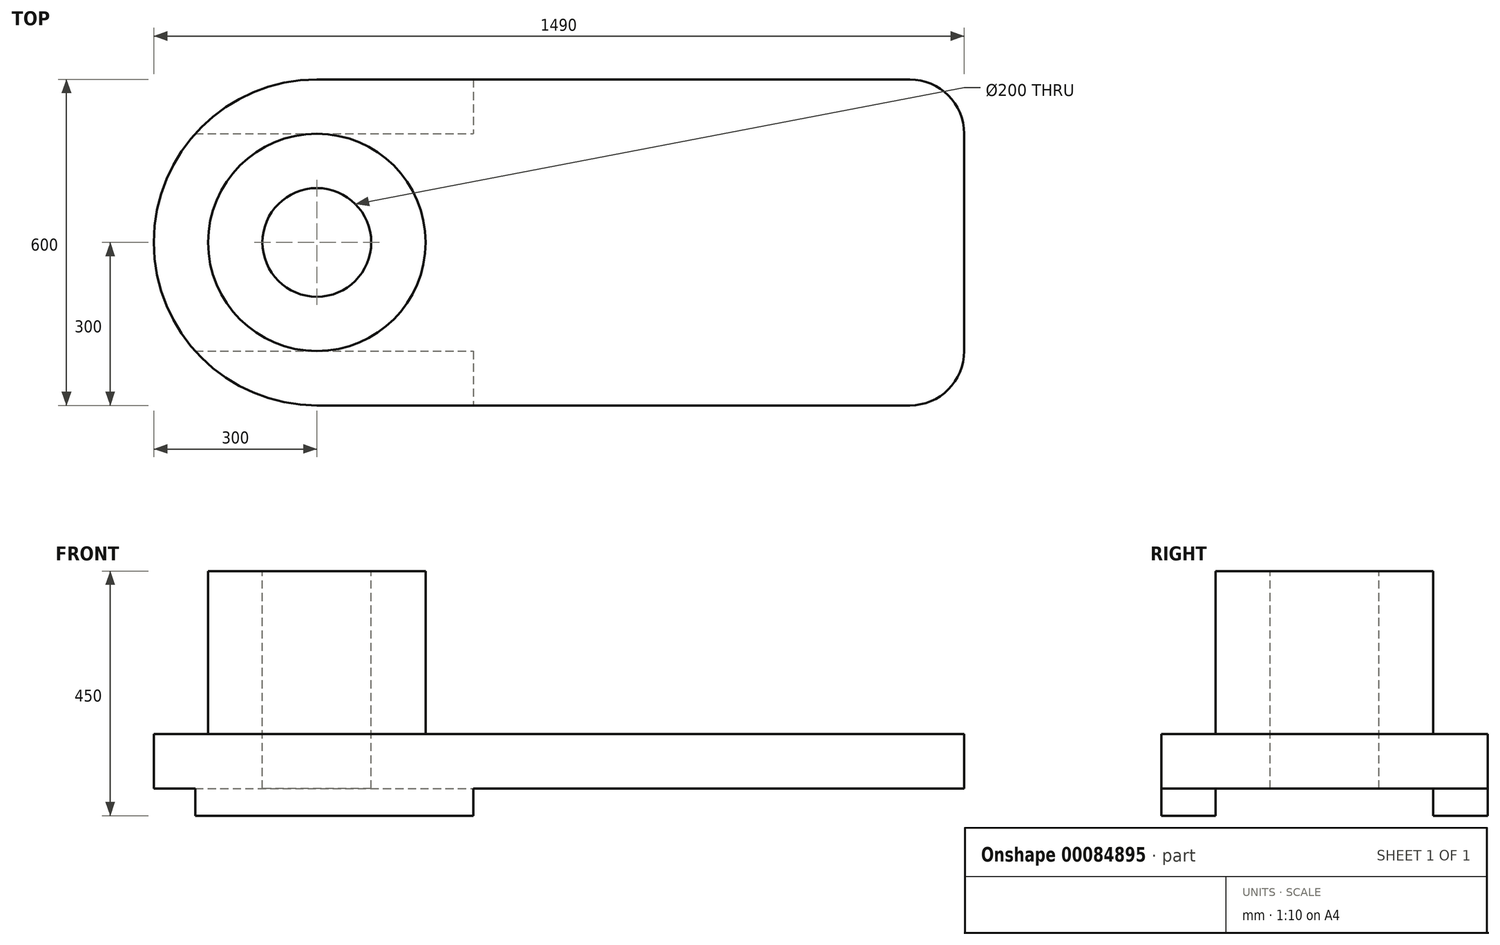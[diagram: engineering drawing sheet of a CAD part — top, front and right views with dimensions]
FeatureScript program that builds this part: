
annotation { "Feature Type Name" : "Feature", "Feature Type Description" : "" }
export const myFeature = defineFeature(function(context is Context, id is Id, definition is map)
    precondition{}
    {
        {
            var Q0;
            Q0=qCreatedBy(makeId("Top.planeOp"),FACE);
            var sketch = newSketch(context, id + "F0", { "sketchPlane" : qUnion([Q0])});
            skLineSegment(sketch, "E0.bottom", {"start": v(-595, -300) * mm, "end": v(495, -300) * mm});
            skLineSegment(sketch, "E0.top", {"start": v(-595, 300) * mm, "end": v(495, 300) * mm});
            skLineSegment(sketch, "E0.right", {"start": v(595, -200) * mm, "end": v(595, 200) * mm});
            skPoint(sketch, "E0.middle", {"position": v(0, 0) * mm});
            skArc(sketch, "E1", {"start": v(-595, 300) * mm, "mid": v(-895, 0) * mm, "end": v(-595, -300) * mm});
            skPoint(sketch, "E2.visualSharp", {"position": v(595, 300) * mm});
            skArc(sketch, "E2.filletArc", {"start": v(595, 200) * mm, "mid": v(565.71, 270.71) * mm, "end": v(495, 300) * mm});
            skPoint(sketch, "E3.visualSharp", {"position": v(595, -300) * mm});
            skArc(sketch, "E3.filletArc", {"start": v(495, -300) * mm, "mid": v(565.71, -270.71) * mm, "end": v(595, -200) * mm});
            skSolve(sketch);
        }
        {
            var Q0;
            Q0 = qSketchRegion(id + "F0", true);
            extrude(context, id + "F1", {"entities" : qUnion([Q0]), "depth" : 100 * mm});
        }
        {
            var Q0;
            Q0=makeQuery(id+"F1.opExtrude","CAP_FACE",FACE,{"disambiguationData":[OSD([sQuery(id+"F0.wireOp",EDGE,"E0.bottom"),sQuery(id+"F0.wireOp",EDGE,"E0.top"),sQuery(id+"F0.wireOp",EDGE,"E0.right"),sQuery(id+"F0.wireOp",EDGE,"E1"),sQuery(id+"F0.wireOp",EDGE,"E2.filletArc"),sQuery(id+"F0.wireOp",EDGE,"E3.filletArc")])],"isStart":true});
            var sketch = newSketch(context, id + "F2", { "sketchPlane" : qUnion([Q0])});
            skLineSegment(sketch, "E4.bottom", {"start": v(-818.6, -200) * mm, "end": v(-307.27, -200) * mm});
            skLineSegment(sketch, "E4.top", {"start": v(-818.6, 200) * mm, "end": v(-307.27, 200) * mm});
            skPoint(sketch, "E4.middle", {"position": v(0, 0) * mm});
            skPoint(sketch, "E5.middle", {"position": v(595, 0) * mm});
            skLineSegment(sketch, "E6", {"start": v(-307.27, -300) * mm, "end": v(-595, -300) * mm});
            skLineSegment(sketch, "E7", {"start": v(-307.27, 300) * mm, "end": v(-595, 300) * mm});
            skArc(sketch, "E8", {"start": v(-595, 300) * mm, "mid": v(-895, 0) * mm, "end": v(-595, -300) * mm});
            skPoint(sketch, "E5.bottom.start.orphan", {"position": v(-307.27, -553.53) * mm});
            skPoint(sketch, "E5.right.start.orphan", {"position": v(1497.27, -553.53) * mm});
            skPoint(sketch, "E5.top.end.orphan", {"position": v(1497.27, 553.53) * mm});
            skPoint(sketch, "E9.orphan", {"position": v(-307.27, 553.53) * mm});
            skPoint(sketch, "E4.left.start.orphan", {"position": v(-1096.29, -200) * mm});
            skPoint(sketch, "E10.orphan", {"position": v(-1096.29, 200) * mm});
            skLineSegment(sketch, "E11", {"start": v(-307.27, -300) * mm, "end": v(-307.27, -200) * mm});
            skLineSegment(sketch, "E12", {"start": v(-307.27, 200) * mm, "end": v(-307.27, 300) * mm});
            skPoint(sketch, "E13.orphan", {"position": v(1096.29, 200) * mm});
            skPoint(sketch, "E14.orphan", {"position": v(1096.29, -200) * mm});
            skSolve(sketch);
        }
        {
            var Q0;
            Q0 = qSketchRegion(id + "F2", true);
            extrude(context, id + "F3", {"entities" : qUnion([Q0]), "operationType" : NewBodyOperationType.ADD, "depth" : 50 * mm});
        }
        {
            var Q0;
            Q0=makeQuery(id+"F1.opExtrude","CAP_FACE",FACE,{"disambiguationData":[OSD([sQuery(id+"F0.wireOp",EDGE,"E0.bottom"),sQuery(id+"F0.wireOp",EDGE,"E0.top"),sQuery(id+"F0.wireOp",EDGE,"E0.right"),sQuery(id+"F0.wireOp",EDGE,"E1"),sQuery(id+"F0.wireOp",EDGE,"E2.filletArc"),sQuery(id+"F0.wireOp",EDGE,"E3.filletArc")])],"isStart":false});
            var sketch = newSketch(context, id + "F4", { "sketchPlane" : qUnion([Q0])});
            skCircle(sketch, "E15", {"center": v(-595, 0) * mm, "radius": 200 * mm});
            skLineSegment(sketch, "E16", {"start": v(-507.82, 180) * mm, "end": v(253.11, 180) * mm});
            skLineSegment(sketch, "E17", {"start": v(283.11, 210) * mm, "end": v(283.11, 300) * mm});
            skLineSegment(sketch, "E18", {"start": v(-407.65, 70) * mm, "end": v(363.11, 70) * mm});
            skLineSegment(sketch, "E19", {"start": v(393.11, 100) * mm, "end": v(393.11, 300) * mm});
            skLineSegment(sketch, "E20", {"start": v(-507.82, -180) * mm, "end": v(253.11, -180) * mm});
            skLineSegment(sketch, "E21", {"start": v(283.11, -210) * mm, "end": v(283.11, -300) * mm});
            skLineSegment(sketch, "E22", {"start": v(-407.65, -70) * mm, "end": v(363.11, -70) * mm});
            skLineSegment(sketch, "E23", {"start": v(393.11, -100) * mm, "end": v(393.11, -300) * mm});
            skPoint(sketch, "E24.visualSharp", {"position": v(283.11, -180) * mm});
            skArc(sketch, "E24.filletArc", {"start": v(283.11, -210) * mm, "mid": v(274.32, -188.79) * mm, "end": v(253.11, -180) * mm});
            skPoint(sketch, "E25.visualSharp", {"position": v(393.11, -70) * mm});
            skArc(sketch, "E25.filletArc", {"start": v(393.11, -100) * mm, "mid": v(384.32, -78.79) * mm, "end": v(363.11, -70) * mm});
            skPoint(sketch, "E26.visualSharp", {"position": v(393.11, 70) * mm});
            skArc(sketch, "E26.filletArc", {"start": v(363.11, 70) * mm, "mid": v(384.32, 78.79) * mm, "end": v(393.11, 100) * mm});
            skPoint(sketch, "E27.visualSharp", {"position": v(283.11, 180) * mm});
            skArc(sketch, "E27.filletArc", {"start": v(253.11, 180) * mm, "mid": v(274.32, 188.79) * mm, "end": v(283.11, 210) * mm});
            skSolve(sketch);
        }
        {
            var Q0;
            Q0 = qSketchRegion(id + "F4", true);
            extrude(context, id + "F5", {"entities" : qUnion([Q0]), "operationType" : NewBodyOperationType.ADD, "depth" : 300 * mm});
        }
        {
            var Q0;
            Q0=makeQuery(id+"F5.opExtrude","CAP_FACE",FACE,{"disambiguationData":[OSD([sQuery(id+"F4.wireOp",EDGE,"E15")])],"isStart":false});
            var sketch = newSketch(context, id + "F6", { "sketchPlane" : qUnion([Q0])});
            skCircle(sketch, "E28", {"center": v(-595, 0) * mm, "radius": 100 * mm});
            skSolve(sketch);
        }
        {
            var Q0;
            Q0 = qSketchRegion(id + "F6", true);
            extrude(context, id + "F7", {"entities" : qUnion([Q0]), "operationType" : NewBodyOperationType.REMOVE, "endBound" : BoundingType.THROUGH_ALL, "oppositeDirection" : true, "depth" : 25 * mm});
        }
    });
